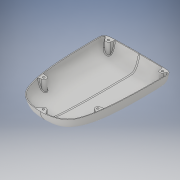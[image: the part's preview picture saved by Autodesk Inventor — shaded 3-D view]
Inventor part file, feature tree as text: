
AUTODESK INVENTOR PART (.ipt)
format: ipt  version: 2019.3 (Build 233278000, 278)  size: 15,695,360 bytes
history: native  units: mm
features: other x19, sketch x5, plane x3, extrude x3, surface_op x3, loft x2, shell x1, mirror x1, fillet x1
ambient origin geometry x8: Origin, YZ Plane, XZ Plane, XY Plane, X Axis, Y Axis, Z Axis, Center Point
bodies: Solid8 (feature_tree)
feature tree (38):
  other  "deck.ipt"
  sketch  "Sketch1"  dims[d15=212.0mm d47=28.0mm d48=145.0mm]
  sketch  "Sketch2"  dims[d107=200.0mm d108=10.0mm]
  sketch  "Sketch3"  dims[d122=84.0mm d130=110.0mm d144=25.0mm]
  other  "Transversal (front)"
  other  "Longitudinal"
  plane  "Work Plane9"
  other  "Transversal (mid)"
  plane  "Work Plane1"
  other  "Transversal (back)"
  plane  "Work Plane7"
  other  "Top"
  loft  "Loft4"
  shell  "Shell1"  Thickness=145.0mm
  extrude  "Extrusion1"  Depth=200.0mm
  mirror  "Mirror1"
  extrude  "Extrusion3"  Depth=110.0mm
  fillet  "Fillet1"  Radius=25.0mm
  extrude  "Extrusion4"  Depth=63.0mm
  other  "Image2"
  other  "Image3"
  other  "Image4"
  other  "Front Profile"
  other  "Srf48"
  other  "Srf49"
  other  "Srf50"
  other  "Edges57"
  other  "Edges58"
  other  "Edges59"
  other  "Edges60"
  other  "Srf51"
  sketch  "Sketch20"  dims[d145=25.0mm d150=63.0mm]
  sketch  "Sketch22"  dims[d190=35.5mm d191=38.8mm d192=39.5mm d193=34.5mm d194=110.0mm d195=200.0mm d196=81.0mm d197=25.0mm d199=20.776473mm d316=3.0mm d321=3.0mm d423=140.0mm d425=205.0mm d429=141.0mm d430=250.0mm d455=57.0mm d460=57.0mm d461=0.0mm d462=90.0deg d463=0.0mm d464=90.0deg d465=0.0mm d466=90.0deg d467=0.0mm d468=90.0deg d472=0.0mm d473=90.0deg d474=0.0mm d475=90.0deg d476=0.0mm d477=90.0deg d478=0.0mm d479=90.0deg d480=1.9mm d481=10.0mm d482=0.0mm d488=3.099267mm d489=3.0mm d509=5.0mm d513=5.0mm d518=5.0mm d519=7.0mm d525=7.0mm d526=7.0mm d528=4.0mm d532=4.0mm d533=4.0mm d538=5.0mm d539=4.0mm d540=7.0mm d541=5.0mm d542=4.0mm d543=7.0mm d544=10.0mm d545=0.0mm d546=2.0mm d548=0.0mm d549=0.0mm]
  other  "Image5"
  loft  "LoftSrf13"
  surface_op  "Boundary Patch25"
  surface_op  "Boundary Patch26"
  surface_op  "Boundary Patch27"
